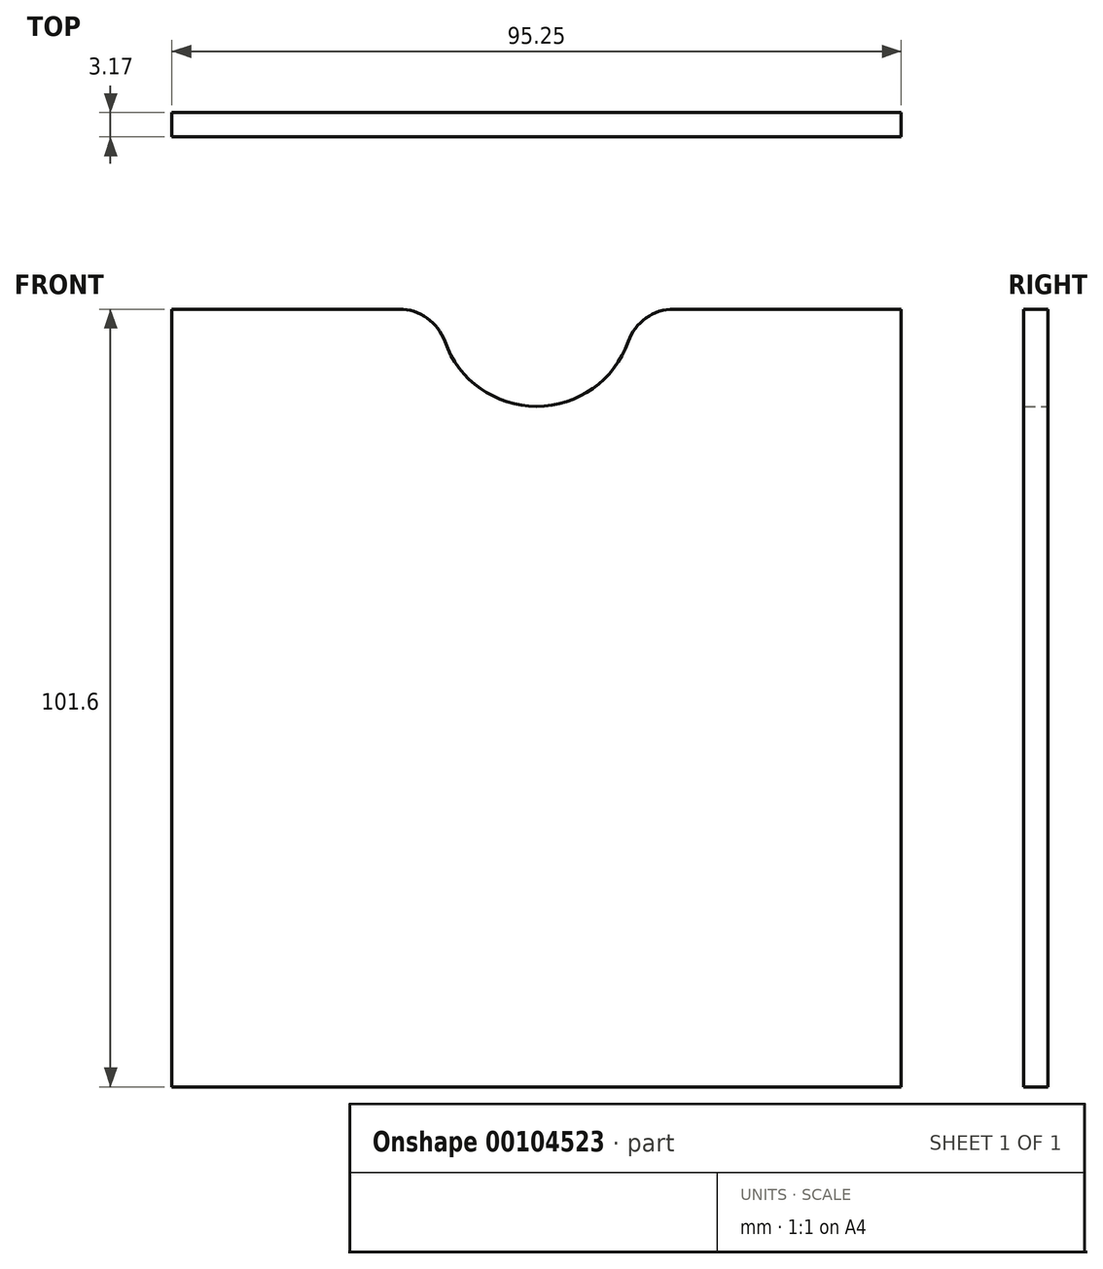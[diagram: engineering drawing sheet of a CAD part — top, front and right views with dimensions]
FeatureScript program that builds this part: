
annotation { "Feature Type Name" : "Feature", "Feature Type Description" : "" }
export const myFeature = defineFeature(function(context is Context, id is Id, definition is map)
    precondition{}
    {
        {
            var Q0;
            Q0=qCreatedBy(makeId("Front.planeOp"),FACE);
            var sketch = newSketch(context, id + "F0", { "sketchPlane" : qUnion([Q0])});
            skLineSegment(sketch, "E0.bottom", {"start": v(0, 0) * mm, "end": v(95.25, 0) * mm});
            skLineSegment(sketch, "E0.top", {"start": v(0, 101.6) * mm, "end": v(29.66, 101.6) * mm});
            skLineSegment(sketch, "E0.left", {"start": v(0, 0) * mm, "end": v(0, 101.6) * mm});
            skLineSegment(sketch, "E0.right", {"start": v(95.25, 0) * mm, "end": v(95.25, 101.6) * mm});
            skArc(sketch, "E1", {"start": v(35.65, 97.37) * mm, "mid": v(47.62, 88.9) * mm, "end": v(59.6, 97.37) * mm});
            skLineSegment(sketch, "E2.trimOffspring", {"start": v(65.59, 101.6) * mm, "end": v(95.25, 101.6) * mm});
            skPoint(sketch, "E3.visualSharp", {"position": v(34.92, 101.6) * mm});
            skArc(sketch, "E3.filletArc", {"start": v(35.65, 97.37) * mm, "mid": v(33.33, 100.43) * mm, "end": v(29.66, 101.6) * mm});
            skPoint(sketch, "E4.visualSharp", {"position": v(60.32, 101.6) * mm});
            skArc(sketch, "E4.filletArc", {"start": v(65.59, 101.6) * mm, "mid": v(61.92, 100.43) * mm, "end": v(59.6, 97.37) * mm});
            skSolve(sketch);
        }
        {
            var Q0;
            Q0 = qSketchRegion(id + "F0", true);
            extrude(context, id + "F1", {"entities" : qUnion([Q0]), "depth" : 3.17 * mm});
        }
    });
